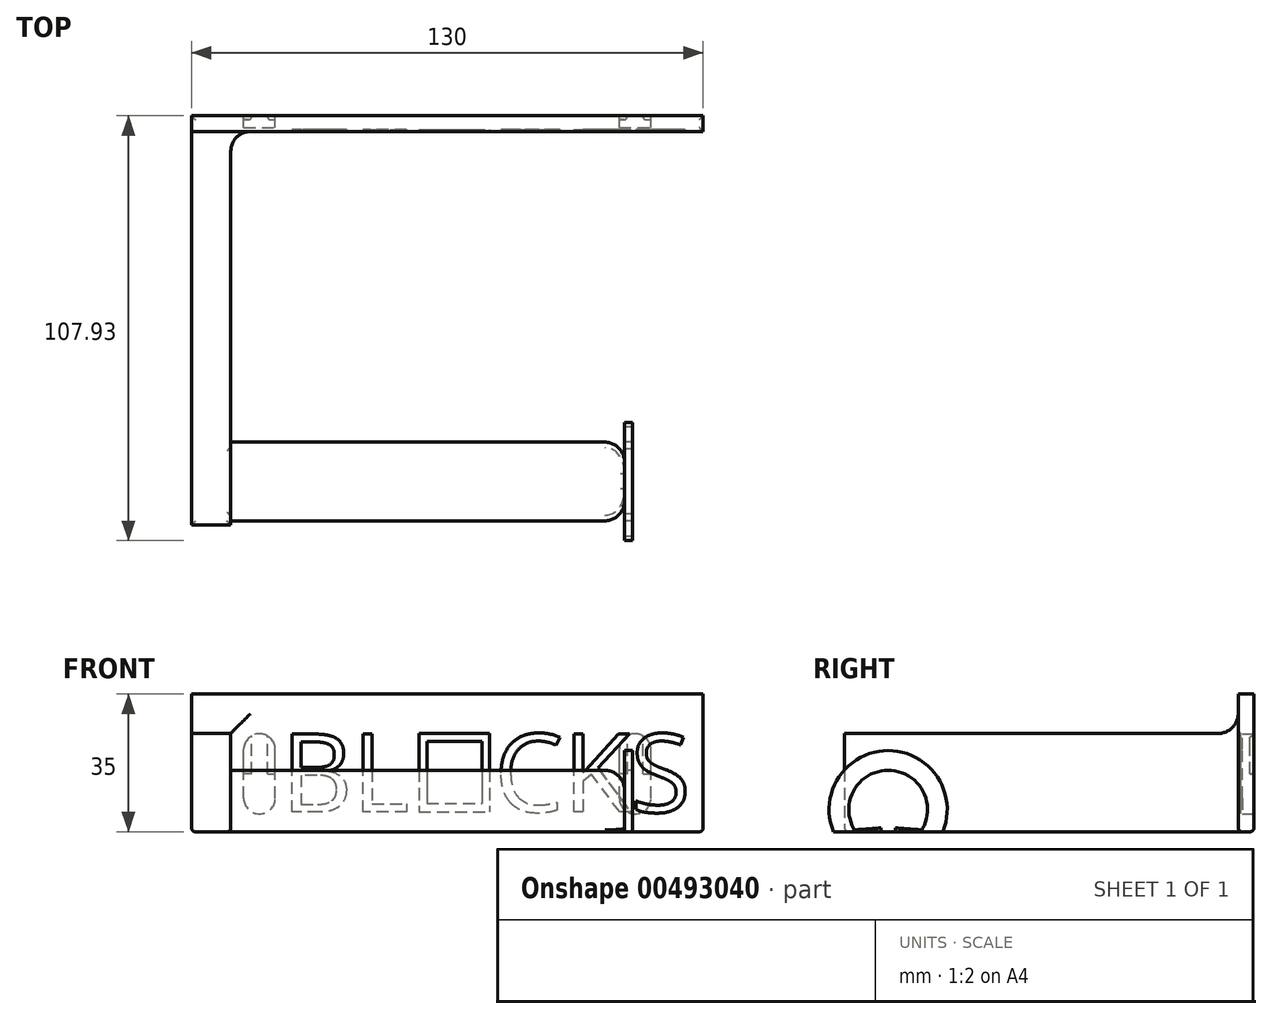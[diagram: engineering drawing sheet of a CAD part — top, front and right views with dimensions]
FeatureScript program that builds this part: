
annotation { "Feature Type Name" : "Feature", "Feature Type Description" : "" }
export const myFeature = defineFeature(function(context is Context, id is Id, definition is map)
    precondition{}
    {
        {
            var Q0;
            Q0=qCreatedBy(makeId("Top.planeOp"),FACE);
            var sketch = newSketch(context, id + "F0", { "sketchPlane" : qUnion([Q0])});
            skLineSegment(sketch, "E0.bottom", {"start": v(-59.05, 53.01) * mm, "end": v(70.95, 53.01) * mm});
            skLineSegment(sketch, "E0.top", {"start": v(-59.05, 49.01) * mm, "end": v(70.95, 49.01) * mm});
            skLineSegment(sketch, "E0.left", {"start": v(-59.05, 53.01) * mm, "end": v(-59.05, 49.01) * mm});
            skLineSegment(sketch, "E0.right", {"start": v(70.95, 53.01) * mm, "end": v(70.95, 49.01) * mm});
            skLineSegment(sketch, "E1.bottom", {"start": v(-59.05, 49.01) * mm, "end": v(-49.05, 49.01) * mm});
            skLineSegment(sketch, "E1.top", {"start": v(-59.05, -50.99) * mm, "end": v(-49.05, -50.99) * mm});
            skLineSegment(sketch, "E1.left", {"start": v(-59.05, 49.01) * mm, "end": v(-59.05, -50.99) * mm});
            skLineSegment(sketch, "E1.right", {"start": v(-49.05, 49.01) * mm, "end": v(-49.05, -50.99) * mm});
            skSolve(sketch);
        }
        {
            var Q0;
            Q0=makeQuery(id+"F0.imprint","IMPRINT",FACE,{"disambiguationData":[TD([[makeQuery(id+"F0.imprint","IMPRINT",EDGE,{"derivedFrom":sQuery(id+"F0.wireOp",EDGE,"E0.bottom")}),-1.0]])]});
            extrude(context, id + "F1", {"entities" : qUnion([Q0]), "depth" : 35 * mm});
        }
        {
            var Q0;
            Q0 = qSketchRegion(id + "F0", true);
            extrude(context, id + "F2", {"entities" : qUnion([Q0]), "operationType" : NewBodyOperationType.ADD, "depth" : 25 * mm});
        }
        {
            var Q0;
            Q0=makeQuery(id+"F1.opExtrude","SWEPT_FACE",FACE,{"disambiguationData":[OSD([sQuery(id+"F0.wireOp",EDGE,"E0.top"),sQuery(id+"F0.wireOp",EDGE,"E1.bottom")])]});
            var sketch = newSketch(context, id + "F3", { "sketchPlane" : qUnion([Q0])});
            skText(sketch, "E2", { "text": "BL   CKS", "fontName": "OpenSans-Regular.ttf"});
            skLineSegment(sketch, "E3.bottom", {"start": v(-1.26, 25) * mm, "end": v(18.6, 25) * mm});
            skLineSegment(sketch, "E3.top", {"start": v(-1.26, 5) * mm, "end": v(18.6, 5) * mm});
            skLineSegment(sketch, "E3.left", {"start": v(-1.26, 25) * mm, "end": v(-1.26, 5) * mm});
            skLineSegment(sketch, "E4.0", {"start": v(0.74, 23) * mm, "end": v(0.74, 7.27) * mm});
            skLineSegment(sketch, "E5", {"start": v(-1.26, 5) * mm, "end": v(16.74, 5) * mm});
            skLineSegment(sketch, "E6", {"start": v(-1.26, 25) * mm, "end": v(16.74, 25) * mm});
            skLineSegment(sketch, "E7", {"start": v(16.74, 25) * mm, "end": v(16.74, 5) * mm});
            skLineSegment(sketch, "E8.0", {"start": v(14.74, 23) * mm, "end": v(14.74, 7.27) * mm});
            skLineSegment(sketch, "E9", {"start": v(0.74, 23) * mm, "end": v(14.74, 23) * mm});
            skLineSegment(sketch, "E10", {"start": v(0.74, 7.27) * mm, "end": v(14.74, 7.27) * mm});
            const initialGuessF3  = {"E2": [-0.03617, 0.005, 1, 0, 0.02]};
            skSetInitialGuess(sketch, initialGuessF3);
            skSolve(sketch);
        }
        {
            var Q0;
            Q0 = qSketchRegion(id + "F3", true);
            extrude(context, id + "F4", {"entities" : qUnion([Q0]), "operationType" : NewBodyOperationType.REMOVE, "oppositeDirection" : true, "depth" : 0.5 * mm});
        }
        {
            var Q0;
            Q0=makeQuery(id+"F2.opExtrude","SWEPT_FACE",FACE,{"disambiguationData":[OSD([sQuery(id+"F0.wireOp",EDGE,"E1.right")])]});
            var sketch = newSketch(context, id + "F5", { "sketchPlane" : qUnion([Q0])});
            skCircle(sketch, "E11", {"center": v(-39.92, 5.63) * mm, "radius": 10 * mm});
            skSolve(sketch);
        }
        {
            var Q0;
            Q0 = qSketchRegion(id + "F5", true);
            extrude(context, id + "F6", {"entities" : qUnion([Q0]), "operationType" : NewBodyOperationType.ADD, "depth" : 100 * mm});
        }
        {
            var Q0;
            {var subQ0=sQuery(id+"F5.wireOp",EDGE,"E11");Q0=makeQuery(id+"F6.boolean.opBoolean","SPLIT",EDGE,{"disambiguationData":[topologyDisambiguationEdgeConnected([makeQuery(id+"F2.opExtrude","SWEPT_FACE",FACE,{"disambiguationData":[OSD([sQuery(id+"F0.wireOp",EDGE,"E1.right")])]})])],"derivedFrom":makeQuery(id+"F6.opExtrude","CAP_EDGE",EDGE,{"disambiguationData":[OSD([subQ0])],"isStart":true})});}
            fillet(context, id + "F7", {"entities" : qUnion([Q0]), "radius" : 3 * mm, "tangentPropagation" : true, "allowEdgeOverflow" : false});
        }
        {
            var Q0;
            {var subQ0=sQuery(id+"F0.wireOp",EDGE,"E0.top");Q0=makeQuery(id+"F2.boolean.opBoolean","INTERSECT",EDGE,{"derivedFrom":[makeQuery(id+"F1.opExtrude","SWEPT_FACE",FACE,{"disambiguationData":[OSD([subQ0,sQuery(id+"F0.wireOp",EDGE,"E1.bottom")])]}),makeQuery(id+"F2.opExtrude","CAP_FACE",FACE,{"disambiguationData":[OSD([sQuery(id+"F0.wireOp",EDGE,"E0.bottom"),subQ0,sQuery(id+"F0.wireOp",EDGE,"E0.left"),sQuery(id+"F0.wireOp",EDGE,"E0.right"),sQuery(id+"F0.wireOp",EDGE,"E1.top"),sQuery(id+"F0.wireOp",EDGE,"E1.left"),sQuery(id+"F0.wireOp",EDGE,"E1.right")])],"isStart":false})]});}
            var Q1;
            Q1=makeQuery(id+"F2.opExtrude","SWEPT_EDGE",EDGE,{"disambiguationData":[OSD([sQuery(id+"F0.wireOp",EDGE,"E0.top"),sQuery(id+"F0.wireOp",EDGE,"E1.bottom"),sQuery(id+"F0.wireOp",EDGE,"E1.right")])]});
            fillet(context, id + "F8", {"entities" : qUnion([Q0, Q1]), "radius" : 5 * mm, "tangentPropagation" : true, "allowEdgeOverflow" : false});
        }
        {
            var Q0;
            Q0=makeQuery(id+"F6.opExtrude","CAP_FACE",FACE,{"disambiguationData":[OSD([sQuery(id+"F5.wireOp",EDGE,"E11")])],"isStart":false});
            var sketch = newSketch(context, id + "F9", { "sketchPlane" : qUnion([Q0])});
            skLineSegment(sketch, "E12.bottom", {"start": v(-51.71, 0) * mm, "end": v(-25.04, 0) * mm});
            skLineSegment(sketch, "E12.top", {"start": v(-51.71, -10.52) * mm, "end": v(-25.04, -10.52) * mm});
            skLineSegment(sketch, "E12.left", {"start": v(-51.71, 0) * mm, "end": v(-51.71, -10.52) * mm});
            skLineSegment(sketch, "E12.right", {"start": v(-25.04, 0) * mm, "end": v(-25.04, -10.52) * mm});
            skSolve(sketch);
        }
        {
            var Q0;
            Q0=makeQuery(id+"F9.imprint","IMPRINT",FACE,{"disambiguationData":[TD([[makeQuery(id+"F9.imprint","IMPRINT",EDGE,{"derivedFrom":sQuery(id+"F9.wireOp",EDGE,"E12.top")}),1.0]])]});
            var Q1;
            {var subQ0=sQuery(id+"F9.wireOp",EDGE,"E12.bottom");var subQ1=makeQuery(id+"F6.opExtrude","CAP_EDGE",EDGE,{"disambiguationData":[OSD([sQuery(id+"F5.wireOp",EDGE,"E11")])],"isStart":false});var subQ2=makeQuery(id+"F9.imprint","INTERSECT",VERTEX,{"disambiguationData":[OD(0.0)],"derivedFrom":[subQ1,subQ0]});Q1=makeQuery(id+"F9.imprint","IMPRINT",FACE,{"disambiguationData":[TD([[makeQuery(id+"F9.imprint","IMPRINT",EDGE,{"disambiguationData":[TD([[subQ2,-1.0]])],"derivedFrom":subQ0}),-1.0]])]});}
            extrude(context, id + "F10", {"entities" : qUnion([Q0, Q1]), "operationType" : NewBodyOperationType.REMOVE, "oppositeDirection" : true, "depth" : 200 * mm});
        }
        {
            var Q0;
            Q0=makeQuery(id+"F6.opExtrude","CAP_FACE",FACE,{"disambiguationData":[OSD([sQuery(id+"F5.wireOp",EDGE,"E11")])],"isStart":false});
            var sketch = newSketch(context, id + "F11", { "sketchPlane" : qUnion([Q0])});
            skCircle(sketch, "E13", {"center": v(-39.92, 5.63) * mm, "radius": 15 * mm});
            skSolve(sketch);
        }
        {
            var Q0;
            Q0=makeQuery(id+"F11.imprint","IMPRINT",FACE,{"disambiguationData":[TD([[makeQuery(id+"F11.imprint","IMPRINT",EDGE,{"derivedFrom":sQuery(id+"F11.wireOp",EDGE,"nWVQnvLN-VFYT-Tghe-joRu-gpZlYB4faa90")}),1.0]])]});
            var Q1;
            Q1=makeQuery(id+"F11.imprint","IMPRINT",FACE,{"disambiguationData":[TD([[makeQuery(id+"F11.imprint","IMPRINT",EDGE,{"derivedFrom":makeQuery(id+"F10.boolean.opBoolean","COPY",EDGE,{"derivedFrom":makeQuery(id+"F10.opExtrude","CAP_EDGE",EDGE,{"disambiguationData":[OSD([sQuery(id+"F9.wireOp",EDGE,"E12.bottom")])],"isStart":true})})}),1.0]])]});
            var Q2;
            Q2=makeQuery(id+"F11.imprint","IMPRINT",FACE,{"disambiguationData":[TD([[makeQuery(id+"F11.imprint","IMPRINT",EDGE,{"derivedFrom":sQuery(id+"F11.wireOp",EDGE,"E13")}),1.0]])]});
            extrude(context, id + "F12", {"entities" : qUnion([Q0, Q1, Q2]), "operationType" : NewBodyOperationType.ADD, "depth" : 2 * mm});
        }
        {
            var Q0;
            Q0=makeQuery(id+"F12.opExtrude","CAP_FACE",FACE,{"disambiguationData":[OSD([sQuery(id+"F11.wireOp",EDGE,"E13")])],"isStart":false});
            var sketch = newSketch(context, id + "F13", { "sketchPlane" : qUnion([Q0])});
            skLineSegment(sketch, "E14.bottom", {"start": v(-58.28, 0) * mm, "end": v(-16.94, 0) * mm});
            skLineSegment(sketch, "E14.top", {"start": v(-58.28, -15.08) * mm, "end": v(-16.94, -15.08) * mm});
            skLineSegment(sketch, "E14.left", {"start": v(-58.28, 0) * mm, "end": v(-58.28, -15.08) * mm});
            skLineSegment(sketch, "E14.right", {"start": v(-16.94, 0) * mm, "end": v(-16.94, -15.08) * mm});
            skSolve(sketch);
        }
        {
            var Q0;
            Q0=makeQuery(id+"F13.imprint","IMPRINT",FACE,{"disambiguationData":[TD([[makeQuery(id+"F13.imprint","IMPRINT",EDGE,{"derivedFrom":sQuery(id+"F13.wireOp",EDGE,"E14.top")}),1.0]])]});
            var Q1;
            {var subQ0=sQuery(id+"F13.wireOp",EDGE,"E14.bottom");var subQ1=makeQuery(id+"F12.opExtrude","CAP_EDGE",EDGE,{"disambiguationData":[OSD([sQuery(id+"F11.wireOp",EDGE,"E13")])],"isStart":false});var subQ2=makeQuery(id+"F13.imprint","INTERSECT",VERTEX,{"disambiguationData":[OD(0.0)],"derivedFrom":[subQ1,subQ0]});Q1=makeQuery(id+"F13.imprint","IMPRINT",FACE,{"disambiguationData":[TD([[makeQuery(id+"F13.imprint","IMPRINT",EDGE,{"disambiguationData":[TD([[subQ2,-1.0]])],"derivedFrom":subQ0}),-1.0]])]});}
            extrude(context, id + "F14", {"entities" : qUnion([Q0, Q1]), "operationType" : NewBodyOperationType.REMOVE, "oppositeDirection" : true, "depth" : 25 * mm});
        }
        {
            var Q0;
            Q0=makeQuery(id+"F6.opExtrude","CAP_EDGE",EDGE,{"disambiguationData":[OSD([sQuery(id+"F5.wireOp",EDGE,"E11")])],"isStart":false});
            fillet(context, id + "F15", {"entities" : qUnion([Q0]), "radius" : 5 * mm, "tangentPropagation" : true, "allowEdgeOverflow" : false});
        }
        {
            var Q0;
            Q0=makeQuery(id+"F1.opExtrude","SWEPT_FACE",FACE,{"disambiguationData":[OSD([sQuery(id+"F0.wireOp",EDGE,"E0.bottom")])]});
            var sketch = newSketch(context, id + "F16", { "sketchPlane" : qUnion([Q0])});
            skLineSegment(sketch, "E15.0", {"start": v(59.05, 35) * mm, "end": v(-70.95, 35) * mm});
            skLineSegment(sketch, "E16", {"start": v(-53.66, 8.53) * mm, "end": v(-53.66, 20.9) * mm, "construction": true});
            skArc(sketch, "E17.0.startCap", {"start": v(-49.66, 8.53) * mm, "mid": v(-53.66, 4.53) * mm, "end": v(-57.66, 8.53) * mm});
            skArc(sketch, "E17.0.endCap", {"start": v(-57.66, 20.9) * mm, "mid": v(-53.66, 24.9) * mm, "end": v(-49.66, 20.9) * mm});
            skLineSegment(sketch, "E17.0.left", {"start": v(-57.66, 8.53) * mm, "end": v(-57.66, 20.9) * mm});
            skLineSegment(sketch, "E17.0.right", {"start": v(-49.66, 8.53) * mm, "end": v(-49.66, 20.9) * mm});
            skLineSegment(sketch, "E18", {"start": v(-5.95, 35) * mm, "end": v(-5.95, -6.83) * mm, "construction": true});
            skLineSegment(sketch, "E19.MirrorCS", {"start": v(37.77, 8.53) * mm, "end": v(37.77, 20.9) * mm});
            skArc(sketch, "E20.MirrorCS", {"start": v(45.77, 20.9) * mm, "mid": v(41.77, 24.9) * mm, "end": v(37.77, 20.9) * mm});
            skLineSegment(sketch, "E21.MirrorCS", {"start": v(45.77, 8.53) * mm, "end": v(45.77, 20.9) * mm});
            skLineSegment(sketch, "E22.MirrorCS", {"start": v(41.77, 8.53) * mm, "end": v(41.77, 20.9) * mm, "construction": true});
            skArc(sketch, "E23.MirrorCS", {"start": v(37.77, 8.53) * mm, "mid": v(41.77, 4.53) * mm, "end": v(45.77, 8.53) * mm});
            skSolve(sketch);
        }
        {
            var Q0;
            Q0 = qSketchRegion(id + "F16", true);
            extrude(context, id + "F17", {"entities" : qUnion([Q0]), "operationType" : NewBodyOperationType.REMOVE, "oppositeDirection" : true, "depth" : 3 * mm});
        }
        {
            var Q0;
            Q0=makeQuery(id+"F1.opExtrude","SWEPT_FACE",FACE,{"disambiguationData":[OSD([sQuery(id+"F0.wireOp",EDGE,"E0.bottom")])]});
            var sketch = newSketch(context, id + "F18", { "sketchPlane" : qUnion([Q0])});
            skLineSegment(sketch, "E24.0", {"start": v(59.05, 35) * mm, "end": v(-70.95, 35) * mm, "construction": true});
            skLineSegment(sketch, "E25", {"start": v(-5.95, 35) * mm, "end": v(-5.95, -6.88) * mm, "construction": true});
            skLineSegment(sketch, "E26", {"start": v(-53.66, 24.9) * mm, "end": v(-53.66, 2.58) * mm, "construction": true});
            skPoint(sketch, "E26.endSnap0", {"position": v(-53.66, 4.53) * mm});
            skArc(sketch, "E27.0", {"start": v(-57.66, 20.9) * mm, "mid": v(-53.66, 24.9) * mm, "end": v(-49.66, 20.9) * mm});
            skLineSegment(sketch, "E28.0", {"start": v(-57.66, 14.72) * mm, "end": v(-57.66, 20.9) * mm});
            skLineSegment(sketch, "E29.0", {"start": v(-49.66, 14.72) * mm, "end": v(-49.66, 20.9) * mm});
            skPoint(sketch, "E30.orphan", {"position": v(-57.66, 8.53) * mm});
            skPoint(sketch, "E31.orphan", {"position": v(-49.66, 8.53) * mm});
            skLineSegment(sketch, "E32", {"start": v(-55.66, 14.72) * mm, "end": v(-55.66, 24.37) * mm});
            skLineSegment(sketch, "E33", {"start": v(-55.66, 14.72) * mm, "end": v(-57.66, 14.72) * mm});
            skLineSegment(sketch, "E34.MirrorCS", {"start": v(-51.66, 14.72) * mm, "end": v(-51.66, 24.37) * mm});
            skLineSegment(sketch, "E35.MirrorCS", {"start": v(-51.66, 14.72) * mm, "end": v(-49.66, 14.72) * mm});
            skLineSegment(sketch, "E36.MirrorCS", {"start": v(43.77, 14.72) * mm, "end": v(45.77, 14.72) * mm});
            skLineSegment(sketch, "E37.MirrorCS", {"start": v(39.77, 14.72) * mm, "end": v(37.77, 14.72) * mm});
            skArc(sketch, "E38.MirrorCS", {"start": v(45.77, 20.9) * mm, "mid": v(41.77, 24.9) * mm, "end": v(37.77, 20.9) * mm});
            skLineSegment(sketch, "E39.MirrorCS", {"start": v(39.77, 14.72) * mm, "end": v(39.77, 24.37) * mm});
            skLineSegment(sketch, "E40.MirrorCS", {"start": v(43.77, 14.72) * mm, "end": v(43.77, 24.37) * mm});
            skLineSegment(sketch, "E41.MirrorCS", {"start": v(45.77, 14.72) * mm, "end": v(45.77, 20.9) * mm});
            skLineSegment(sketch, "E42.MirrorCS", {"start": v(37.77, 14.72) * mm, "end": v(37.77, 20.9) * mm});
            skSolve(sketch);
        }
        {
            var Q0;
            Q0 = qSketchRegion(id + "F18", true);
            extrude(context, id + "F19", {"entities" : qUnion([Q0]), "operationType" : NewBodyOperationType.ADD, "oppositeDirection" : true, "depth" : 1 * mm});
        }
        {
            var Q0;
            Q0=makeQuery(id+"F19.opExtrude","CAP_EDGE",EDGE,{"disambiguationData":[OSD([sQuery(id+"F18.wireOp",EDGE,"E41.MirrorCS")])],"isStart":false});
            var Q1;
            Q1=makeQuery(id+"F19.opExtrude","CAP_EDGE",EDGE,{"disambiguationData":[OSD([sQuery(id+"F18.wireOp",EDGE,"E40.MirrorCS")])],"isStart":false});
            var Q2;
            Q2=makeQuery(id+"F19.opExtrude","CAP_EDGE",EDGE,{"disambiguationData":[OSD([sQuery(id+"F18.wireOp",EDGE,"E39.MirrorCS")])],"isStart":false});
            var Q3;
            {var subQ0=sQuery(id+"F18.wireOp",EDGE,"E38.MirrorCS");Q3=makeQuery(id+"F19.opExtrude","CAP_EDGE",EDGE,{"disambiguationData":[OSD([subQ0]),TDD([makeQuery(id+"F18.imprint","IMPRINT",EDGE,{"disambiguationData":[TD([[makeQuery(id+"F18.imprint","INTERSECT",VERTEX,{"derivedFrom":[subQ0,sQuery(id+"F18.wireOp",EDGE,"E42.MirrorCS")]}),1.0]])],"derivedFrom":subQ0})])],"isStart":false});}
            var Q4;
            Q4=makeQuery(id+"F19.opExtrude","CAP_EDGE",EDGE,{"disambiguationData":[OSD([sQuery(id+"F18.wireOp",EDGE,"E34.MirrorCS")])],"isStart":false});
            var Q5;
            Q5=makeQuery(id+"F19.opExtrude","CAP_EDGE",EDGE,{"disambiguationData":[OSD([sQuery(id+"F18.wireOp",EDGE,"E29.0")])],"isStart":false});
            var Q6;
            {var subQ0=sQuery(id+"F18.wireOp",EDGE,"E27.0");Q6=makeQuery(id+"F19.opExtrude","CAP_EDGE",EDGE,{"disambiguationData":[OSD([subQ0]),TDD([makeQuery(id+"F18.imprint","IMPRINT",EDGE,{"disambiguationData":[TD([[makeQuery(id+"F18.imprint","INTERSECT",VERTEX,{"derivedFrom":[subQ0,sQuery(id+"F18.wireOp",EDGE,"E28.0")]}),-1.0]])],"derivedFrom":subQ0})])],"isStart":false});}
            var Q7;
            Q7=makeQuery(id+"F19.opExtrude","CAP_EDGE",EDGE,{"disambiguationData":[OSD([sQuery(id+"F18.wireOp",EDGE,"E32")])],"isStart":false});
            fillet(context, id + "F20", {"entities" : qUnion([Q0, Q1, Q2, Q3, Q4, Q5, Q6, Q7]), "radius" : 0.8 * mm, "tangentPropagation" : true, "allowEdgeOverflow" : false});
        }
        {
            var Q0;
            {var subQ0=sQuery(id+"F0.wireOp",EDGE,"E0.right");var subQ1=sQuery(id+"F0.wireOp",EDGE,"E0.left");var subQ2=sQuery(id+"F0.wireOp",EDGE,"E0.top");var subQ3=sQuery(id+"F0.wireOp",EDGE,"E0.bottom");Q0=makeQuery(id+"F14.boolean.opBoolean","MERGE",FACE,{"derivedFrom":[makeQuery(id+"F10.boolean.opBoolean","MERGE",FACE,{"derivedFrom":[makeQuery(id+"F2.boolean.opBoolean","MERGE",FACE,{"derivedFrom":[makeQuery(id+"F1.opExtrude","CAP_FACE",FACE,{"disambiguationData":[OSD([subQ3,subQ2,subQ1,subQ0,sQuery(id+"F0.wireOp",EDGE,"E1.bottom")])],"isStart":true}),makeQuery(id+"F2.opExtrude","CAP_FACE",FACE,{"disambiguationData":[OSD([subQ3,subQ2,subQ1,subQ0,sQuery(id+"F0.wireOp",EDGE,"E1.top"),sQuery(id+"F0.wireOp",EDGE,"E1.left"),sQuery(id+"F0.wireOp",EDGE,"E1.right")])],"isStart":true})]}),makeQuery(id+"F10.opExtrude","SWEPT_FACE",FACE,{"disambiguationData":[OSD([sQuery(id+"F9.wireOp",EDGE,"E12.bottom")])]})]}),makeQuery(id+"F14.opExtrude","SWEPT_FACE",FACE,{"disambiguationData":[OSD([sQuery(id+"F13.wireOp",EDGE,"E14.bottom")])]})]});}
            fillet(context, id + "F21", {"entities" : qUnion([Q0]), "radius" : 1 * mm, "tangentPropagation" : true, "allowEdgeOverflow" : false});
        }
    });
